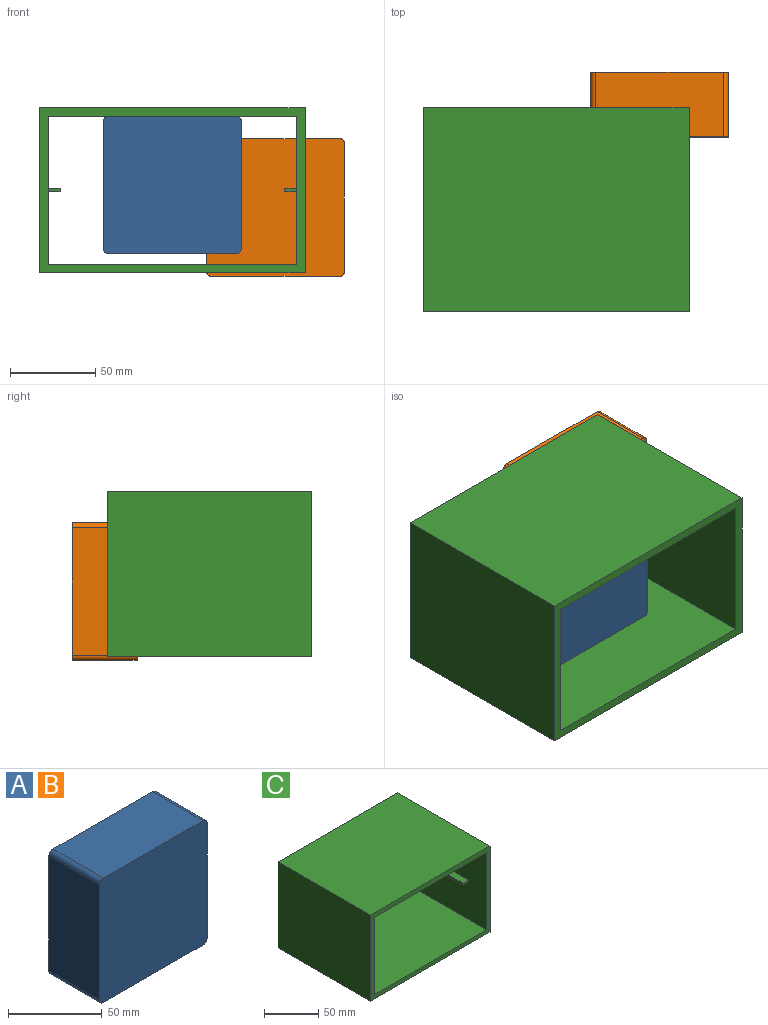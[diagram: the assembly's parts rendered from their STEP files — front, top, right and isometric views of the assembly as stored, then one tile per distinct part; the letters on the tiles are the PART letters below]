
ASSEMBLY  parts=3 mates=1
PART A: 10 faces, bbox 81x38x81 mm
  f0: plane 75x38mm, normal (0,0,-1), area 2850mm2, adj f4,f5,f6,f9
  f1: plane 75x38mm, normal (1,0,0), area 2850mm2, adj f4,f5,f6,f7
  f2: plane 75x38mm, normal (0,0,1), area 2850mm2, adj f4,f5,f7,f8
  f3: plane 75x38mm, normal (-1,0,0), area 2850mm2, adj f4,f5,f8,f9
  f4: plane 81x81mm, normal (0,-1,0), area 6553.3mm2, adj f0,f1,f2,f3,f6,f7,f8,f9
  f5: plane 81x81mm, normal (0,1,0), area 6553.3mm2, adj f0,f1,f2,f3,f6,f7,f8,f9
  f6: cylinder r=3mm len=38mm, axis (0,-1,0), area 179.1mm2, adj f0,f1,f4,f5
  f7: cylinder r=3mm len=38mm, axis (0,1,0), area 179.1mm2, adj f1,f2,f4,f5
  f8: cylinder r=3mm len=38mm, axis (0,-1,0), area 179.1mm2, adj f2,f3,f4,f5
  f9: cylinder r=3mm len=38mm, axis (0,1,0), area 179.1mm2, adj f0,f3,f4,f5
PART B: same geometry as A
PART C: 20 faces, bbox 156x120x97 mm
  f0: plane 120x97mm, normal (-1,0,0), area 11640mm2, adj f1,f7,f8,f9
  f1: plane 156x120mm, normal (0,0,-1), area 18720mm2, adj f0,f2,f8,f9
  f2: plane 120x97mm, normal (1,0,0), area 11640mm2, adj f1,f7,f8,f9
  f3: plane 120x87mm, normal (-1,0,0), area 10400mm2, adj f4,f6,f8,f9,f15,f17,f18,f19
  f4: plane 146x120mm, normal (0,0,1), area 17520mm2, adj f3,f5,f8,f9
  f5: plane 120x87mm, normal (1,0,0), area 10400mm2, adj f4,f6,f8,f9,f10,f11,f13,f14
  f6: plane 146x120mm, normal (0,0,-1), area 17520mm2, adj f3,f5,f8,f9
  f7: plane 156x120mm, normal (0,0,1), area 18720mm2, adj f0,f2,f8,f9
  f8: plane 156x97mm, normal (0,1,0), area 2430mm2, adj f0,f1,f2,f3,f4,f5,f6,f7
  f9: plane 156x97mm, normal (0,-1,0), area 2430mm2, adj f0,f1,f2,f3,f4,f5,f6,f7
  f10: plane 7x2mm, normal (0,1,0), area 14mm2, adj f5,f12,f13,f14
  f11: plane 7x2mm, normal (0,-1,0), area 14mm2, adj f5,f12,f13,f14
  f12: plane 20x2mm, normal (1,0,0), area 40mm2, adj f10,f11,f13,f14
  f13: plane 20x7mm, normal (0,0,1), area 140mm2, adj f5,f10,f11,f12
  f14: plane 20x7mm, normal (0,0,-1), area 140mm2, adj f5,f10,f11,f12
  f15: plane 7x2mm, normal (0,1,0), area 14mm2, adj f3,f16,f18,f19
  f16: plane 20x2mm, normal (-1,0,0), area 40mm2, adj f15,f17,f18,f19
  f17: plane 7x2mm, normal (0,-1,0), area 14mm2, adj f3,f16,f18,f19
  f18: plane 20x7mm, normal (0,0,1), area 140mm2, adj f3,f15,f16,f17
  f19: plane 20x7mm, normal (0,0,-1), area 140mm2, adj f3,f15,f16,f17
PLACE A t=(-45.07,-36.57,12.49)mm
PLACE B t=(15.55,25.05,-0.79)mm
PLACE C rot(axis=(0,0,1),180deg) t=(-45.07,4.43,9.49)mm
MATE parallel C.f6 <-> A.f2  axis (0,0,-1) through (-45.07,-55.57,52.99)mm
